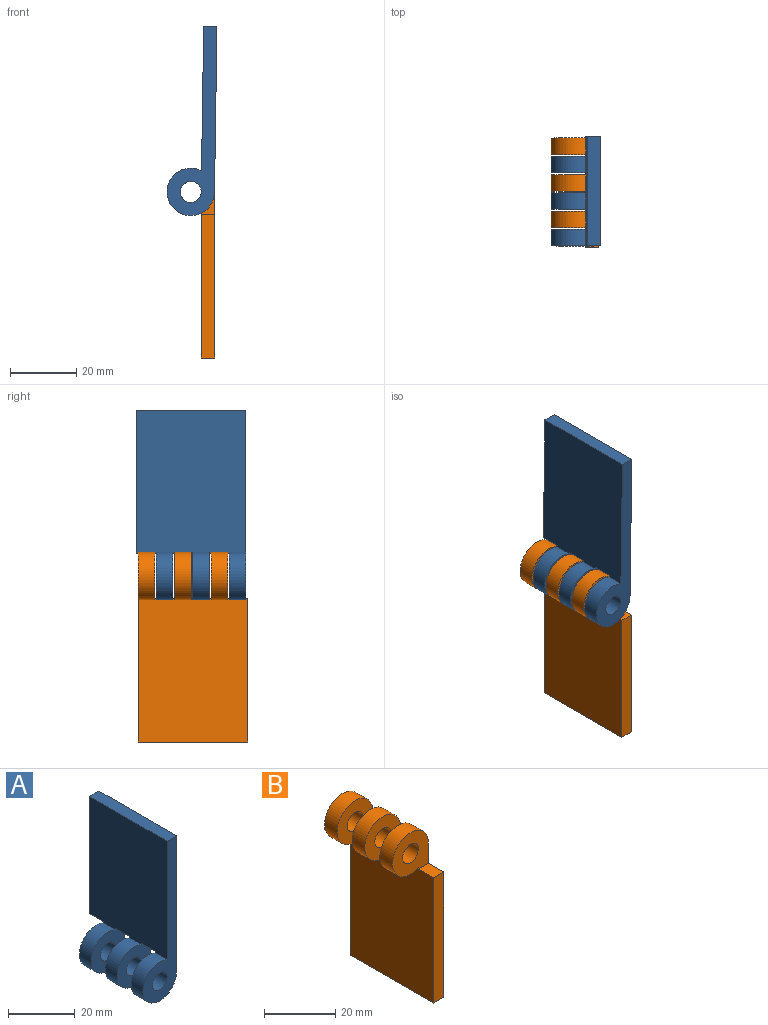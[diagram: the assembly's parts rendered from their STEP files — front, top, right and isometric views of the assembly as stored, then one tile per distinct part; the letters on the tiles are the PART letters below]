
ASSEMBLY  parts=2 mates=1
PART A: 19 faces, bbox 14.3x33x57.2 mm
  f0: plane 43.58x33mm, normal (-1,0,0), area 1429.2mm2, adj f1,f3,f5,f6,f7,f8,f9,f11
  f1: cylinder r=7.15mm len=14.3mm, axis (0,1,0), area 184.8mm2, adj f0,f2,f5,f6
  f2: plane 50x33mm, normal (1,0,0), area 1525.5mm2, adj f1,f3,f5,f6,f7,f8,f9,f11
  f3: plane 33x4mm, normal (0,0,1), area 132mm2, adj f0,f2,f8,f16
  f4: cylinder r=3.15mm len=6.3mm, axis (0,1,0), area 99mm2, adj f5,f6
  f5: plane 14.3x14.3mm, normal (0,-1,0), area 138.7mm2, adj f0,f1,f2,f4,f13
  f6: plane 14.3x14.3mm, normal (0,1,0), area 138.7mm2, adj f0,f1,f2,f4,f7
  f7: plane 6x4mm, normal (0,0,-1), area 24mm2, adj f0,f2,f6,f8
  f8: plane 43.08x4mm, normal (0,1,0), area 172.3mm2, adj f0,f2,f3,f7
  f9: cylinder r=7.15mm len=14.3mm, axis (0,1,0), area 184.8mm2, adj f0,f2,f11,f12
  f10: cylinder r=3.15mm len=6.3mm, axis (0,1,0), area 99mm2, adj f11,f12
  f11: plane 14.3x14.3mm, normal (0,-1,0), area 138.7mm2, adj f0,f2,f9,f10,f18
  f12: plane 14.3x14.3mm, normal (0,1,0), area 138.7mm2, adj f0,f2,f9,f10,f13
  f13: plane 6x4mm, normal (0,0,-1), area 24mm2, adj f0,f2,f5,f12
  f14: cylinder r=7.15mm len=14.3mm, axis (0,1,0), area 184.8mm2, adj f0,f2,f16,f17
  f15: cylinder r=3.15mm len=6.3mm, axis (0,1,0), area 99mm2, adj f16,f17
  f16: plane 57.15x14.3mm, normal (0,-1,0), area 311.1mm2, adj f0,f2,f3,f14,f15
  f17: plane 14.3x14.3mm, normal (0,1,0), area 138.7mm2, adj f0,f2,f14,f15,f18
  f18: plane 6x4mm, normal (0,0,-1), area 24mm2, adj f0,f2,f11,f17
PART B: 19 faces, bbox 14.3x33x57.2 mm
  f0: plane 14.3x14.3mm, normal (0,1,0), area 138.7mm2, adj f1,f2,f4,f5,f13
  f1: cylinder r=7.15mm len=14.3mm, axis (0,1,0), area 184.8mm2, adj f0,f2,f5,f6
  f2: plane 43.58x33mm, normal (-1,0,0), area 1429.2mm2, adj f0,f1,f3,f6,f7,f8,f9,f10
  f3: plane 33x4mm, normal (0,0,-1), area 132mm2, adj f2,f5,f8,f17
  f4: cylinder r=3.15mm len=6.3mm, axis (0,1,0), area 99mm2, adj f0,f6
  f5: plane 50x33mm, normal (1,0,0), area 1525.5mm2, adj f0,f1,f3,f6,f7,f8,f9,f10
  f6: plane 14.3x14.3mm, normal (0,-1,0), area 138.7mm2, adj f1,f2,f4,f5,f7
  f7: plane 6x4mm, normal (0,0,1), area 24mm2, adj f2,f5,f6,f8
  f8: plane 43.08x4mm, normal (0,-1,0), area 172.3mm2, adj f2,f3,f5,f7
  f9: plane 14.3x14.3mm, normal (0,1,0), area 138.7mm2, adj f2,f5,f10,f11,f18
  f10: cylinder r=7.15mm len=14.3mm, axis (0,1,0), area 184.8mm2, adj f2,f5,f9,f12
  f11: cylinder r=3.15mm len=6.3mm, axis (0,1,0), area 99mm2, adj f9,f12
  f12: plane 14.3x14.3mm, normal (0,-1,0), area 138.7mm2, adj f2,f5,f10,f11,f13
  f13: plane 6x4mm, normal (0,0,1), area 24mm2, adj f0,f2,f5,f12
  f14: cylinder r=7.15mm len=14.3mm, axis (0,1,0), area 184.8mm2, adj f2,f5,f16,f17
  f15: cylinder r=3.15mm len=6.3mm, axis (0,1,0), area 99mm2, adj f16,f17
  f16: plane 14.3x14.3mm, normal (0,-1,0), area 138.7mm2, adj f2,f5,f14,f15,f18
  f17: plane 57.15x14.3mm, normal (0,1,0), area 311.1mm2, adj f2,f3,f5,f14,f15
  f18: plane 6x4mm, normal (0,0,1), area 24mm2, adj f2,f5,f9,f16
PLACE A rot(axis=(0,1,0),0.9deg) t=(0.49,16.5,-13.77)mm
PLACE B t=(0.49,0,-13.66)mm fixed
MATE revolute B.f4 <-> A.f4  axis (0,1,0) through (-6.66,6,-13.66)mm
